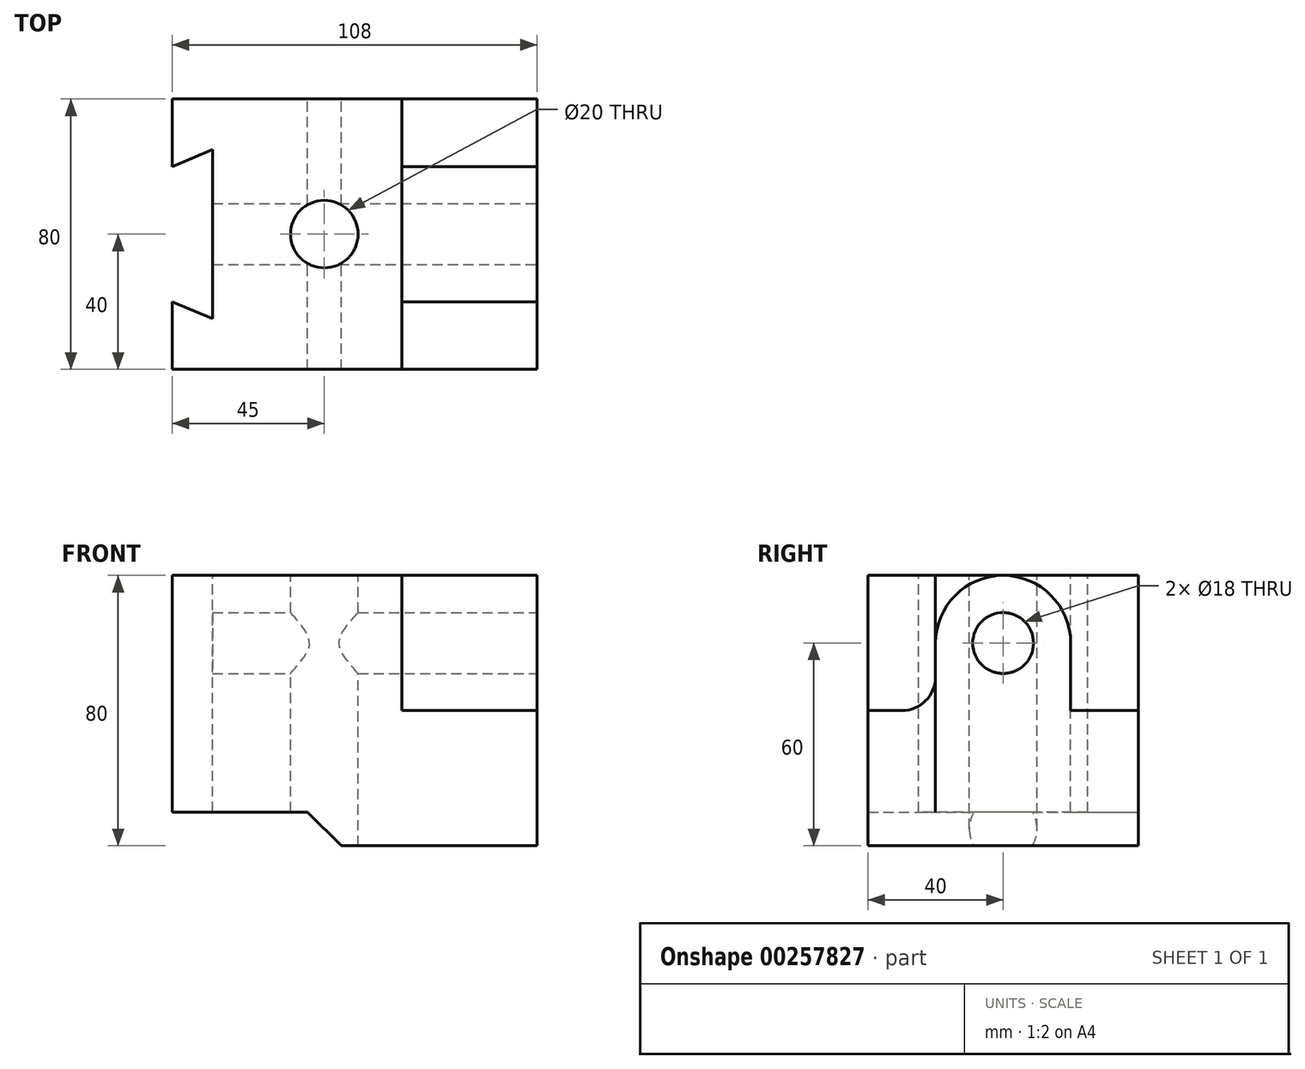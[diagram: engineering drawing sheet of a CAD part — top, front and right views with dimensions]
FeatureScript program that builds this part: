
annotation { "Feature Type Name" : "Feature", "Feature Type Description" : "" }
export const myFeature = defineFeature(function(context is Context, id is Id, definition is map)
    precondition{}
    {
        {
            var Q0;
            Q0=qCreatedBy(makeId("Front.planeOp"),FACE);
            var sketch = newSketch(context, id + "F0", { "sketchPlane" : qUnion([Q0])});
            skLineSegment(sketch, "E0", {"start": v(0, 0) * mm, "end": v(58, 0) * mm});
            skLineSegment(sketch, "E1", {"start": v(58, 0) * mm, "end": v(58, 40) * mm});
            skLineSegment(sketch, "E2", {"start": v(18, 80) * mm, "end": v(-50, 80) * mm});
            skLineSegment(sketch, "E3", {"start": v(-50, 80) * mm, "end": v(-50, 10) * mm});
            skLineSegment(sketch, "E4", {"start": v(-50, 10) * mm, "end": v(-10, 10) * mm});
            skLineSegment(sketch, "E5", {"start": v(-10, 10) * mm, "end": v(0, 0) * mm});
            skLineSegment(sketch, "E6", {"start": v(58, 40) * mm, "end": v(18, 40) * mm});
            skLineSegment(sketch, "E7", {"start": v(18, 40) * mm, "end": v(18, 80) * mm});
            skSolve(sketch);
        }
        {
            var Q0;
            Q0 = qSketchRegion(id + "F0", true);
            extrude(context, id + "F1", {"entities" : qUnion([Q0]), "endBound" : BoundingType.SYMMETRIC, "depth" : 80 * mm});
        }
        {
            var Q0;
            Q0=makeQuery(id+"F1.opExtrude","SWEPT_FACE",FACE,{"disambiguationData":[OSD([sQuery(id+"F0.wireOp",EDGE,"E1")])]});
            var sketch = newSketch(context, id + "F2", { "sketchPlane" : qUnion([Q0])});
            skCircle(sketch, "E8", {"center": v(0, 60) * mm, "radius": 9 * mm});
            skArc(sketch, "E9", {"start": v(20, 60) * mm, "mid": v(0, 80) * mm, "end": v(-20, 60) * mm});
            skLineSegment(sketch, "E10", {"start": v(-40, 40) * mm, "end": v(-20, 40) * mm});
            skLineSegment(sketch, "E11", {"start": v(40, 40) * mm, "end": v(40, 0) * mm});
            skLineSegment(sketch, "E12", {"start": v(40, 0) * mm, "end": v(-40, 0) * mm});
            skLineSegment(sketch, "E13", {"start": v(-40, 0) * mm, "end": v(-40, 40) * mm});
            skLineSegment(sketch, "E14", {"start": v(20, 60) * mm, "end": v(-22.92, 60) * mm, "construction": true});
            skLineSegment(sketch, "E15", {"start": v(-20, 60) * mm, "end": v(-20, 40) * mm});
            skLineSegment(sketch, "E16", {"start": v(20, 60) * mm, "end": v(20, 40) * mm});
            skLineSegment(sketch, "E17.trimOffspring", {"start": v(20, 40) * mm, "end": v(40, 40) * mm});
            skSolve(sketch);
        }
        {
            var Q0;
            Q0 = qSketchRegion(id + "F2", true);
            extrude(context, id + "F3", {"entities" : qUnion([Q0]), "operationType" : NewBodyOperationType.ADD, "oppositeDirection" : true, "depth" : 40 * mm});
        }
        {
            var Q0;
            Q0=makeQuery(id+"F3.boolean.opBoolean","SPLIT",FACE,{"disambiguationData":[TD([makeQuery(id+"F3.opExtrude","SWEPT_FACE",FACE,{"disambiguationData":[OSD([sQuery(id+"F2.wireOp",EDGE,"E8")])]})])],"derivedFrom":makeQuery(id+"F1.opExtrude","SWEPT_FACE",FACE,{"disambiguationData":[OSD([sQuery(id+"F0.wireOp",EDGE,"E7")])]})});
            var sketch = newSketch(context, id + "F4", { "sketchPlane" : qUnion([Q0])});
            skCircle(sketch, "E18", {"center": v(0, 60) * mm, "radius": 9 * mm});
            skSolve(sketch);
        }
        {
            var Q0;
            Q0 = qSketchRegion(id + "F4", true);
            extrude(context, id + "F5", {"entities" : qUnion([Q0]), "oppositeDirection" : true, "depth" : 132.5 * mm});
        }
        {
            var Q0;
            Q0=makeQuery(id+"F1.opExtrude","SWEPT_FACE",FACE,{"disambiguationData":[OSD([sQuery(id+"F0.wireOp",EDGE,"E2")])]});
            var sketch = newSketch(context, id + "F6", { "sketchPlane" : qUnion([Q0])});
            skLineSegment(sketch, "E19", {"start": v(-50, 0) * mm, "end": v(-50, 20) * mm});
            skLineSegment(sketch, "E20", {"start": v(-50, 20) * mm, "end": v(-38, 25) * mm});
            skLineSegment(sketch, "E21", {"start": v(-38, 25) * mm, "end": v(-38, -25) * mm});
            skLineSegment(sketch, "E22", {"start": v(-38, -25) * mm, "end": v(-50, -20) * mm});
            skLineSegment(sketch, "E23", {"start": v(-50, -20) * mm, "end": v(-50, 0) * mm});
            skCircle(sketch, "E24", {"center": v(-5, 0) * mm, "radius": 10 * mm});
            skSolve(sketch);
        }
        {
            var Q0;
            Q0=makeQuery(id+"F6.imprint","IMPRINT",FACE,{"disambiguationData":[TD([[makeQuery(id+"F6.imprint","IMPRINT",EDGE,{"derivedFrom":sQuery(id+"F6.wireOp",EDGE,"E19")}),-1.0]])]});
            var Q1;
            Q1=makeQuery(id+"F6.imprint","IMPRINT",FACE,{"disambiguationData":[TD([[makeQuery(id+"F6.imprint","IMPRINT",EDGE,{"derivedFrom":sQuery(id+"F6.wireOp",EDGE,"E24")}),1.0]])]});
            extrude(context, id + "F7", {"entities" : qUnion([Q0, Q1]), "oppositeDirection" : true, "depth" : 100 * mm});
        }
        {
            var Q0;
            Q0=makeQuery(id+"F5.opExtrude","SWEPT_BODY",BODY,{"disambiguationData":[OSD([sQuery(id+"F4.wireOp",EDGE,"E18")])]});
            var Q1;
            Q1=makeQuery(id+"F7.opExtrude","SWEPT_BODY",BODY,{"disambiguationData":[OSD([sQuery(id+"F6.wireOp",EDGE,"E19"),sQuery(id+"F6.wireOp",EDGE,"E20"),sQuery(id+"F6.wireOp",EDGE,"E21"),sQuery(id+"F6.wireOp",EDGE,"E22"),sQuery(id+"F6.wireOp",EDGE,"E23")])]});
            var Q2;
            Q2=makeQuery(id+"F7.opExtrude","SWEPT_BODY",BODY,{"disambiguationData":[OSD([sQuery(id+"F6.wireOp",EDGE,"E24")])]});
            var Q3;
            Q3=makeQuery(id+"F1.opExtrude","SWEPT_BODY",BODY,{"disambiguationData":[OSD([sQuery(id+"F0.wireOp",EDGE,"E0"),sQuery(id+"F0.wireOp",EDGE,"E1"),sQuery(id+"F0.wireOp",EDGE,"E2"),sQuery(id+"F0.wireOp",EDGE,"E3"),sQuery(id+"F0.wireOp",EDGE,"E4"),sQuery(id+"F0.wireOp",EDGE,"E5"),sQuery(id+"F0.wireOp",EDGE,"E6"),sQuery(id+"F0.wireOp",EDGE,"E7")])]});
            booleanBodies(context, id + "F8", {"operationType" : BooleanOperationType.SUBTRACTION, "tools" : qUnion([Q0, Q1, Q2]), "targets" : qUnion([Q3])});
        }
        {
            var Q0;
            Q0=makeQuery(id+"F3.opExtrude","SWEPT_EDGE",EDGE,{"disambiguationData":[OSD([sQuery(id+"F0.wireOp",EDGE,"E1"),sQuery(id+"F0.wireOp",EDGE,"E6"),sQuery(id+"F2.wireOp",EDGE,"E10"),sQuery(id+"F2.wireOp",EDGE,"E15")])]});
            var Q1;
            Q1=makeQuery(id+"F3.opExtrude","SWEPT_EDGE",EDGE,{"disambiguationData":[OSD([sQuery(id+"F0.wireOp",EDGE,"E1"),sQuery(id+"F0.wireOp",EDGE,"E6"),sQuery(id+"F2.wireOp",EDGE,"E16"),sQuery(id+"F2.wireOp",EDGE,"E17.trimOffspring")])]});
            fillet(context, id + "F9", {"entities" : qUnion([Q0, Q1]), "radius" : 10 * mm, "tangentPropagation" : true, "allowEdgeOverflow" : false});
        }
    });
